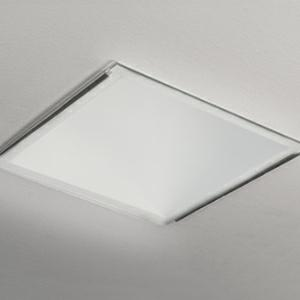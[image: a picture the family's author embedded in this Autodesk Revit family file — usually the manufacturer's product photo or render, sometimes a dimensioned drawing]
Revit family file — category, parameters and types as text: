
# Revit family: 3f_filippi_-_lucequadro_vs_3f_filippi_-_36576_-_lucequadro_led_2000_ep_vs
name_source: partatom
category: Lighting Fixtures
units: mm (PartAtom-declared; Revit-internal decimal feet)

## family parameters
Cut with Voids When Loaded = No
Host = Face
Light Source = No
Part Type = Normal
Room Calculation Point = No
Round Connector Dimension = Use Diameter
Shared = No

## types (1)
- 3F Filippi - Lucequadro VS (1 x LED, 2291 lm, 21 W, 4000 K)
    Apparent Load = 21 VA
    Approval mark = ENEC
    CIE Flux Codes = 79 96 99 100 100
    Color Rendering = 80
    Color Temperature = 4000 K
    Control Gear = Electronic ballast
    Default Elevation = 1800 mm
    Description = ILLUMINOTECHNICAL
Luminous efficiency 100% (DLOR 100%, ULOR 0%).
Initial luminous flux of the luminaire 2291 lm.
Emergency luminaire luminous flux BLF 20%.
Direct symmetric distribution.
Installation Interdistance Transv.D = 0.83 x hu - Long.D = 0.80 x hu.
Average luminance <3000 cd/m² for radial angles >65°.
Tabular UGR (CIE 117 - 4H-8H; S=0.25H; 70/50/20): RUG 17.2 - 17.
Beam angle: 58° - 57°.
Luminous efficacy 109 lm/W.
Lifetime (L90/B10): 30000 h. (tq+25°C)
Lifetime (L85/B10): 50000 h. (tq+25°C)
Lifetime (L70/B10): 80000 h. (tq+25°C)
Sudden decreased luminous flux after 50000 hours: 0% (C0).
Photobiological safety in compliance with IEC/TR 62778: RG1 low risk, (IEC 62471).
In compliance with IEC/EN 62722-2-1 - IEC/EN 62717 standards.

SOURCE
Compact LED module 2000/840.
Energy efficiency class (UE 2019/2020 - UE 2019/2015): D.
CIE 13.3 Colour rendering index: CRI >80 (R9 <50%).
IES TM-30 Fidelity Index: Rf = 84 Rg = 95.
CCT nominal colour temperature 4000 K.
Colour initial tolerance (MacAdam): SDCM 3.
Zhaga Book 3 compliant.

MECHANICAL
Housing in white painted steel.
Passive heat dissipator in anodised aluminium, oversized, for optimum thermal management of the LED module.
Flow recuperator in specular aluminium with superficial titanium-magnesium treatment, non-iridescent.
Moulded tempered anti-glare non-combustible glass, thickness 4 mm.
Lock-in mounting of the glass in the lateral seats in specular aluminium.
Fixing brackets in galvanised steel.
Slot-cover polycarbonate casings.
Dimensions: 235x235 mm, height 116 mm. Weight 3.15 kg.
IP44 protection degree for exposed part, IP20 for recessed part.
Mechanical strength to impacts IK08 (5 joule).
Glow-wire test resistance 960°C.

ELECTRICAL
Wiring on a separate unit.
Halogen Free electronic wiring 230V-50/60Hz, power factor 0.90, THD <25%, constant output current, SELV, class II, 1 driver.
Power of the luminaire 21 W.
CE - IEC 60598-1 - EN 60598-1.
EP maintained emergency wiring on board, 1h duration, 24h recharge; compliant with EN 60598-2-22, excluding high risk areas.
SAFE FLICKER: PstLM=<1 and SVM=<0.4 (IEC TR 61547-1 and IEC TR 63158), to ensure a more comfortable and safe light.
Ambient temperature from +5°C to +25°C.
Temperature class T6 max 85°C.
Relative humidity UR: <85%.

INSTALLATION
Pull-up recessed fitting.
False ceiling carving: 210x210 mm.
All accessories dedicated to this product are available on the Catalog and on our website www.3F-Filippi.com.

ACCESSORIES
A0189 - Pair of reinforcing brackets for mineral fibre, metal and plasterboard panels, height 20 mm.

APPLICATIONS
Transit areas, corridors, commercial environments, display areas, shops and shop windows.

WARNING
Luminaire designed for disposal/recycling at end-of-life.
Replaceable (LED only) light source by a professional. Replaceable control gear by a professional.
    Height = 0 mm  [stored 0 ft]
    Lamp = 1 x LED
    Lamp Light Flux = 2291 lm
    Lamp Power = 21 W
    Lamp count = 1
    Length = 235 mm
    Lifetime = 50000 h
    Luminous efficacy = 109 lm/W
    Manufacturer = 3F Filippi
    ModVariant = No
    Model = 3F Filippi - 36576 - Lucequadro LED 2000 EP VS
    Mounting Place = Ceiling
    Mounting Type = Recessed
    Number of Poles = 1
    OnlyDefault = Yes
    Power Factor = 1
    Product Name = 3F Filippi - Lucequadro VS
    Product group = recessed luminaire
    ProductGroupID = 4
    Protection Class = Protection class II
    Protection Degree = IP 20
    RLX_Detail_Level = 1
    RLX_Emergency_Light_Flux = 0 lm
    RLX_Emergency_Type = 0
    RLX_Emergency_Type_DB = No
    RlxData = <blob elided: 57629 chars, md5=074674de>
    Socket = socket
    Standby Power = 0 W
    System Light Flux = 2291 lm
    System Power = 21 W
    Type Comments = Product without accessories
    Type Image = 3ffilippi_36576.jpg
    URL = http://relux.com
    VarID = ---
    Voltage = 0 V
    Weight = 0.00 kg
    Width = 235 mm

note: [stored X ft] marks values corroborated as IEEE doubles in the binary element streams (Revit-internal decimal feet)

## geometry (parser evidence)
native form markers: Blend x4, Sweep x9
no freeform markers — native parametric forms only
